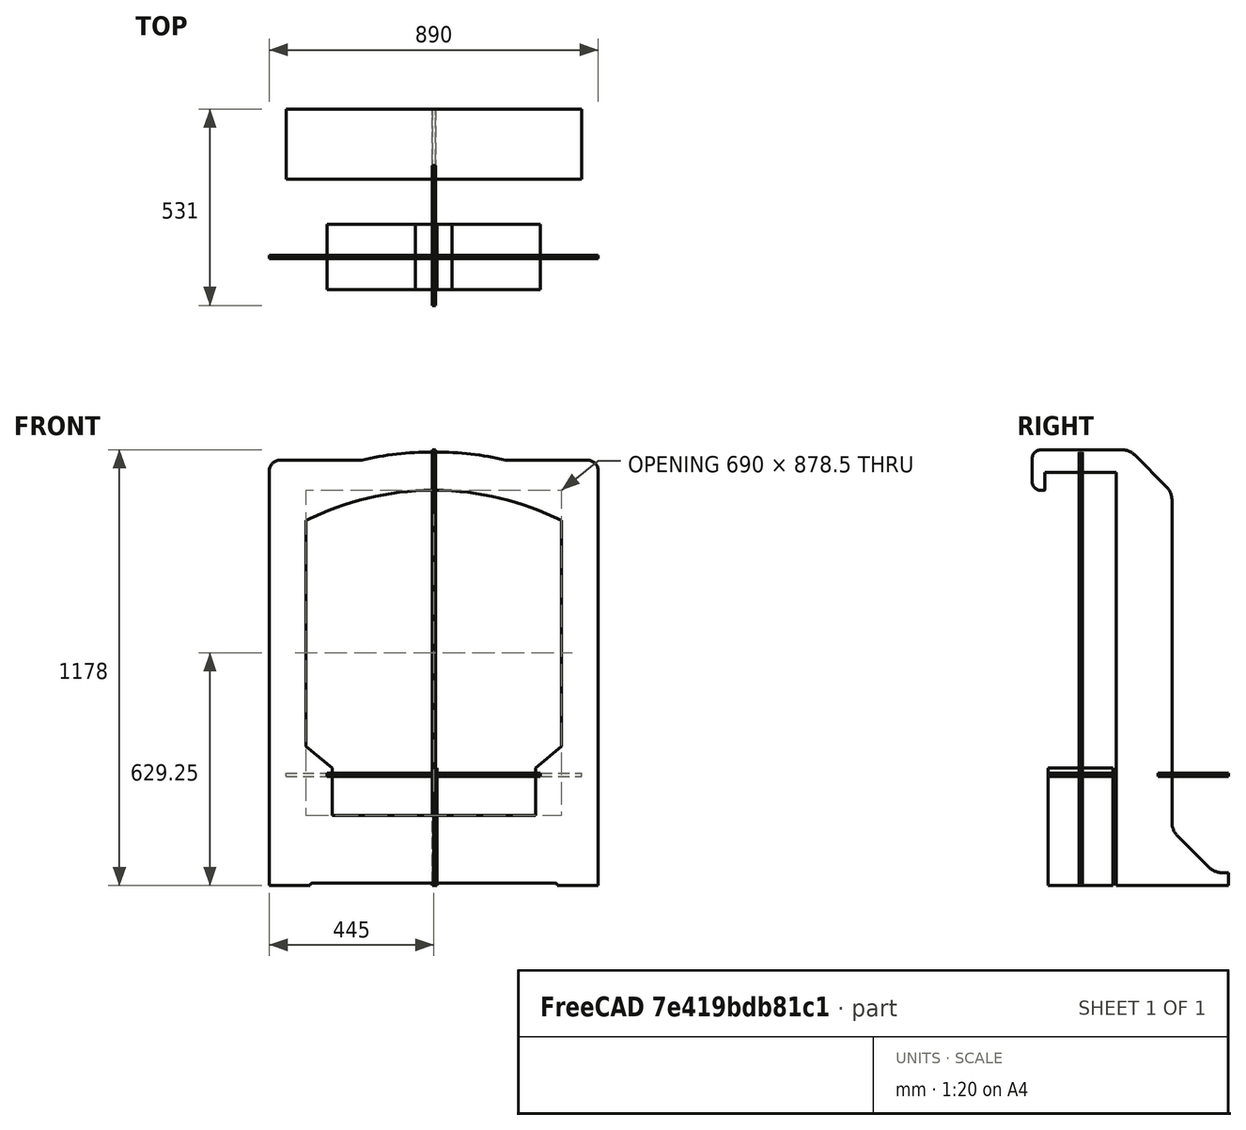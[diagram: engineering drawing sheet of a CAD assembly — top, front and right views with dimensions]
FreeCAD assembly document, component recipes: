
FREECAD ASSEMBLY — COMPONENT RECIPES ("Main_Assembly")

This assembly document has 9 components, labeled P0..P8 below (a component is one placed body or linked part). 8 of them carry a construction recipe — the FreeCAD feature program that regenerates the part from scratch, quoted from this document or its linked companion documents; the rest are supplied as boundary geometry only. No exploded tour is included for this assembly.
COMPONENT P0 — recipe-attached ("Back", modeled in this document).
Construction recipe (the document's own serialized feature program — sketch geometry with constraints, then the solid features built on it; lengths are millimeters unless a unit is written):

FEATURE [PartDesign::CoordinateSystem] LCS_0
  AttacherType = Attacher::AttachEngine3D
  MapMode = 2
  Support = -> [X_Axis002]
FEATURE [Sketcher::SketchObject] Sketch002  label="BackFrame_Sketch"
  FullyConstrained = true
  MapMode = 5
  Placement = pos=(0,0,0) rot=(1,0,0;1.5708rad)
  Support = -> [XZ_Plane002]
  expr: Constraints[57] = <<FrontFrame_Sketch>>.Constraints.height_base_B
  expr: Constraints[2] = 90 - <<key_dimensions>>#<<Dimensions>>.cradle_tilting
  expr: Constraints[66] = <<FrontFrame_Sketch>>.Constraints.foot_width
  expr: Constraints[17] = <<key_dimensions>>#<<Dimensions>>.window_width + <<key_dimensions>>#<<Dimensions>>.frame_width * 2
  expr: Constraints[22] = <<key_dimensions>>#<<Dimensions>>.window_width
  expr: Constraints[70] = <<key_dimensions>>#<<Dimensions>>.cradle_base
  expr: Constraints[33] = <<key_dimensions>>#<<Dimensions>>.top_height
  expr: Constraints[69] = <<key_dimensions>>#<<Dimensions>>.slider_axis_height
  expr: Constraints[8] = <<FrontFrame_Sketch>>.Constraints.lip_width
  expr: Constraints[16] = <<key_dimensions>>#<<Dimensions>>.center_height
  sketch-geometry (26):
    g0: LineSegment StartX=-252.795 StartY=212.12 StartZ=0 EndX=0 EndY=0 EndZ=0
    g1: LineSegment StartX=0 StartY=0 StartZ=0 EndX=252.795 EndY=212.12 EndZ=0
    g2: LineSegment StartX=-275 StartY=-64.25 StartZ=0 EndX=275 EndY=-64.25 EndZ=0
    g3: LineSegment StartX=-275 StartY=-109.25 StartZ=0 EndX=275 EndY=-109.25 EndZ=0
    g4: LineSegment StartX=-126.397 StartY=106.06 StartZ=0 EndX=452.112 EndY=795.5 EndZ=0
    g5: LineSegment StartX=126.397 StartY=106.06 StartZ=0 EndX=-452.112 EndY=795.5 EndZ=0
    g6: LineSegment StartX=-445 StartY=-299.25 StartZ=0 EndX=-334.5 EndY=-299.25 EndZ=0
    g7: ArcOfCircle CenterX=0 CenterY=0 CenterZ=0 NormalX=0 NormalY=0 NormalZ=1 AngleXU=0 Radius=769.25 StartAngle=1.10572 EndAngle=2.03587
    g8: LineSegment StartX=-445 StartY=-299.25 StartZ=0 EndX=-445 EndY=820.75 EndZ=0
    g9: LineSegment StartX=445 StartY=-299.25 StartZ=0 EndX=445 EndY=820.75 EndZ=0
    g10: ArcOfCircle CenterX=0 CenterY=0 CenterZ=0 NormalX=0 NormalY=0 NormalZ=1 AngleXU=0 Radius=872.75 StartAngle=1.34579 EndAngle=1.7958
    g11: LineSegment StartX=-415 StartY=850.75 StartZ=0 EndX=-194.723 EndY=850.75 EndZ=0
    g12: LineSegment StartX=194.723 StartY=850.75 StartZ=0 EndX=415 EndY=850.75 EndZ=0
    g13: GeomPoint X=-445 Y=850.75 Z=0
    g14: ArcOfCircle CenterX=-415 CenterY=820.75 CenterZ=0 NormalX=0 NormalY=0 NormalZ=1 AngleXU=0 Radius=30 StartAngle=1.5708 EndAngle=3.14159
    g15: ArcOfCircle CenterX=415 CenterY=820.75 CenterZ=0 NormalX=0 NormalY=0 NormalZ=1 AngleXU=0 Radius=30 StartAngle=9e-16 EndAngle=1.5708
    g16: LineSegment StartX=-345 StartY=687.547 StartZ=0 EndX=-345 EndY=77.487 EndZ=0
    g17: LineSegment StartX=-345 StartY=77.487 StartZ=0 EndX=-275 EndY=18.75 EndZ=0
    g18: LineSegment StartX=-275 StartY=18.75 StartZ=0 EndX=-275 EndY=-109.25 EndZ=0
    g19: LineSegment StartX=275 StartY=-109.25 StartZ=0 EndX=275 EndY=18.75 EndZ=0
    g20: LineSegment StartX=275 StartY=18.75 StartZ=0 EndX=345 EndY=77.487 EndZ=0
    g21: LineSegment StartX=345 StartY=77.487 StartZ=0 EndX=345 EndY=687.547 EndZ=0
    g22: ArcOfCircle CenterX=-327.5 CenterY=-299.25 CenterZ=0 NormalX=0 NormalY=0 NormalZ=1 AngleXU=0 Radius=7 StartAngle=1.5708 EndAngle=3.14159
    g23: ArcOfCircle CenterX=327.5 CenterY=-299.25 CenterZ=0 NormalX=0 NormalY=0 NormalZ=1 AngleXU=0 Radius=7 StartAngle=3.2e-15 EndAngle=1.5708
    g24: LineSegment StartX=-327.5 StartY=-292.25 StartZ=0 EndX=327.5 EndY=-292.25 EndZ=0
    g25: LineSegment StartX=334.5 StartY=-299.25 StartZ=0 EndX=445 EndY=-299.25 EndZ=0
  constraints (71):
    c: Coincident(g0,g-1)
    c: Distance(g0) = 330
    c: Angle(g-2,g0) = 0.872665
    c: Coincident(g1,g-1)
    c: Symmetric(g0,g1,g-2)
    c: DistanceY(g2,g-1) = 64.25
    c: Equal(g3,g2)
    c: Symmetric(g3,g3,g-2)
    c: DistanceX(g3,g3) = 550
    c: Symmetric(g2,g2,g-2)
    c: Perpendicular(g0,g4)
    c: Symmetric(g0,g-1,g4)
    c: Distance(g4) = 900
    c: Equal(g4,g5)
    c: Perpendicular(g1,g5)
    c: Symmetric(g-1,g1,g5)
    c: DistanceY(g25,g-1) = 299.25
    c: DistanceX(g6,g25) = 890
    c: Symmetric(g6,g25,g-2)
    c: Coincident(g7,g-1)
    c: Radius(g7) = 769.25
    c: Symmetric(g7,g7,g-2)
    c: DistanceX(g7,g7) = 690
    c: Coincident(g8,g6)
    c: Vertical(g8)
    c: Coincident(g9,g25)
    c: Vertical(g9)
    c: Coincident(g10,g-1)
    c: Coincident(g11,g10)
    c: Coincident(g12,g10)
    c: Tangent(g11,g12)
    c: Horizontal(g11)
    c: PointOnObject(g13,g11)
    c: DistanceY(g6,g13) = 1150
    c: Tangent(g8,g14) = 1.5708
    c: Tangent(g11,g14) = 1.5708
    c: Tangent(g12,g15) = 1.5708
    c: Tangent(g9,g15) = -1.5708
    c: Equal(g15,g14)
    c: Radius(g15) = 30
    c: Radius(g10) = 872.75
    c: Coincident(g16,g7)
    c: Vertical(g16)
    c: Coincident(g16,g17)
    c: Coincident(g17,g18)
    c: Coincident(g18,g3)
    c: Coincident(g3,g19)
    c: Vertical(g19)
    c: Coincident(g19,g20)
    c: Coincident(g20,g21)
    c: Coincident(g21,g7)
    c: Vertical(g21)
    c: Vertical(g18)
    c: Equal(g18,g19)
    c: DistanceY(g19,g10) = 109.25
    c: Parallel(g20,g1)
    c: Parallel(g17,g0)
    c: DistanceY(g6,g17) = 318
    c: PointOnObject(g22,g6)
    c: Horizontal(g24)
    c: Tangent(g24,g23) = 1.5708
    c: Tangent(g24,g22) = 1.5708
    c: Coincident(g6,g22)
    c: Coincident(g25,g23)
    c: Tangent(g6,g25)
    c: Symmetric(g22,g23,g-2)
    c: DistanceX(g6,g23) = 669
    c: Radius(g23) = 7
    c: PointOnObject(g13,g8)
    c: DistanceY(g9,g3) = 190
    c: DistanceY(g9,g2) = 235
FEATURE [PartDesign::Pad] Pad001
  Direction = (1,1,1)
  Length = 9
  Length2 = 100
  Midplane = true
  Placement = pos=(0,0,0) rot=(1,0,0;1.5708rad)
  Profile = -> Sketch002
  Type = 0
  expr: Length = <<key_dimensions>>#<<Dimensions>>.MDF_thick
FEATURE [PartDesign::Body] Back
  Group = -> [LCS_0,Sketch002,Pad001]
  Origin = -> Origin002
  Tip = -> Pad001
COMPONENT P1 — recipe-attached ("Back_Reinforcement", modeled in this document).
Construction recipe (the document's own serialized feature program — sketch geometry with constraints, then the solid features built on it; lengths are millimeters unless a unit is written):

FEATURE [PartDesign::CoordinateSystem] LCS_0006
  AttacherType = Attacher::AttachEngine3D
  MapMode = 2
  Support = -> [X_Axis008]
FEATURE [Sketcher::SketchObject] Sketch008
  FullyConstrained = true
  MapMode = 5
  Support = -> [XY_Plane008]
  sketch-geometry (6):
    g0: LineSegment StartX=-399.5 StartY=400 StartZ=0 EndX=399.5 EndY=400 EndZ=0
    g1: LineSegment StartX=399.5 StartY=400 StartZ=0 EndX=399.5 EndY=210 EndZ=0
    g2: LineSegment StartX=399.5 StartY=210 StartZ=0 EndX=-399.5 EndY=210 EndZ=0
    g3: LineSegment StartX=-399.5 StartY=210 StartZ=0 EndX=-399.5 EndY=400 EndZ=0
    g4: GeomPoint X=0 Y=305 Z=0
    g5: GeomPoint X=0 Y=400 Z=0
  constraints (15):
    c: Coincident(g0,g1)
    c: Coincident(g1,g2)
    c: Coincident(g2,g3)
    c: Coincident(g3,g0)
    c: Horizontal(g0)
    c: Horizontal(g2)
    c: Vertical(g1)
    c: Vertical(g3)
    c: PointOnObject(g4,g-2)
    c: Symmetric(g0,g1,g4)
    c: DistanceX(g0,g0) = 799
    c: DistanceY(g1,g1) = 190
    c: PointOnObject(g5,g0)
    c: DistanceY(g-1,g5) = 400
    c: PointOnObject(g5,g-2)
FEATURE [PartDesign::Pad] Pad007
  Direction = (1,1,1)
  Length = 9
  Length2 = 100
  Midplane = true
  Profile = -> Sketch008
  Type = 0
  expr: Length = <<key_dimensions>>#<<Dimensions>>.MDF_thick
FEATURE [PartDesign::Body] Back_Reinforcement
  Group = -> [LCS_0006,Sketch008,Pad007]
  Origin = -> Origin008
  Tip = -> Pad007
COMPONENT P2 — recipe-attached ("Front", modeled in this document).
Construction recipe (the document's own serialized feature program — sketch geometry with constraints, then the solid features built on it; lengths are millimeters unless a unit is written):

FEATURE [Sketcher::SketchObject] Sketch001  label="FrontFrame_Sketch"
  FullyConstrained = true
  MapMode = 5
  Placement = pos=(0,0,0) rot=(1,0,0;1.5708rad)
  Support = -> [XZ_Plane]
  expr: .Constraints.height_base_B = 318mm
  expr: Constraints[70] = <<key_dimensions>>#<<Dimensions>>.cradle_base
  expr: Constraints[22] = <<key_dimensions>>#<<Dimensions>>.window_width
  expr: Constraints[68] = <<key_dimensions>>#<<Dimensions>>.slider_axis_height
  expr: Constraints[16] = <<key_dimensions>>#<<Dimensions>>.center_height
  expr: Constraints[33] = <<key_dimensions>>#<<Dimensions>>.top_height
  expr: Constraints[2] = 90 - <<key_dimensions>>#<<Dimensions>>.cradle_tilting
  sketch-geometry (26):
    g0: LineSegment StartX=-252.795 StartY=212.12 StartZ=0 EndX=0 EndY=0 EndZ=0
    g1: LineSegment StartX=0 StartY=0 StartZ=0 EndX=252.795 EndY=212.12 EndZ=0
    g2: LineSegment StartX=-275 StartY=-64.25 StartZ=0 EndX=275 EndY=-64.25 EndZ=0
    g3: LineSegment StartX=-275 StartY=-109.25 StartZ=0 EndX=275 EndY=-109.25 EndZ=0
    g4: LineSegment StartX=-126.397 StartY=106.06 StartZ=0 EndX=452.112 EndY=795.5 EndZ=0
    g5: LineSegment StartX=126.397 StartY=106.06 StartZ=0 EndX=-452.112 EndY=795.5 EndZ=0
    g6: LineSegment StartX=-445 StartY=-299.25 StartZ=0 EndX=-334.5 EndY=-299.25 EndZ=0
    g7: ArcOfCircle CenterX=0 CenterY=0 CenterZ=0 NormalX=0 NormalY=0 NormalZ=1 AngleXU=0 Radius=769.25 StartAngle=1.10572 EndAngle=2.03587
    g8: LineSegment StartX=-445 StartY=-299.25 StartZ=0 EndX=-445 EndY=820.75 EndZ=0
    g9: LineSegment StartX=445 StartY=-299.25 StartZ=0 EndX=445 EndY=820.75 EndZ=0
    g10: ArcOfCircle CenterX=0 CenterY=0 CenterZ=0 NormalX=0 NormalY=0 NormalZ=1 AngleXU=0 Radius=872.75 StartAngle=1.34579 EndAngle=1.7958
    g11: LineSegment StartX=-415 StartY=850.75 StartZ=0 EndX=-194.723 EndY=850.75 EndZ=0
    g12: LineSegment StartX=194.723 StartY=850.75 StartZ=0 EndX=415 EndY=850.75 EndZ=0
    g13: GeomPoint X=-445 Y=850.75 Z=0
    g14: ArcOfCircle CenterX=-415 CenterY=820.75 CenterZ=0 NormalX=0 NormalY=0 NormalZ=1 AngleXU=0 Radius=30 StartAngle=1.5708 EndAngle=3.14159
    g15: ArcOfCircle CenterX=415 CenterY=820.75 CenterZ=0 NormalX=0 NormalY=0 NormalZ=1 AngleXU=0 Radius=30 StartAngle=1.4e-15 EndAngle=1.5708
    g16: LineSegment StartX=-345 StartY=687.547 StartZ=0 EndX=-345 EndY=77.487 EndZ=0
    g17: LineSegment StartX=-345 StartY=77.487 StartZ=0 EndX=-275 EndY=18.75 EndZ=0
    g18: LineSegment StartX=-275 StartY=18.75 StartZ=0 EndX=-275 EndY=-109.25 EndZ=0
    g19: LineSegment StartX=275 StartY=-109.25 StartZ=0 EndX=275 EndY=18.75 EndZ=0
    g20: LineSegment StartX=275 StartY=18.75 StartZ=0 EndX=345 EndY=77.487 EndZ=0
    g21: LineSegment StartX=345 StartY=77.487 StartZ=0 EndX=345 EndY=687.547 EndZ=0
    g22: ArcOfCircle CenterX=-327.5 CenterY=-299.25 CenterZ=0 NormalX=0 NormalY=0 NormalZ=1 AngleXU=0 Radius=7 StartAngle=1.5708 EndAngle=3.14159
    g23: ArcOfCircle CenterX=327.5 CenterY=-299.25 CenterZ=0 NormalX=0 NormalY=0 NormalZ=1 AngleXU=0 Radius=7 StartAngle=7.8e-15 EndAngle=1.5708
    g24: LineSegment StartX=-327.5 StartY=-292.25 StartZ=0 EndX=327.5 EndY=-292.25 EndZ=0
    g25: LineSegment StartX=334.5 StartY=-299.25 StartZ=0 EndX=445 EndY=-299.25 EndZ=0
  constraints (72):
    c: Coincident(g0,g-1)
    c: Distance(g0) = 330
    c: Angle(g-2,g0) = 0.872665
    c: Coincident(g1,g-1)
    c: Symmetric(g0,g1,g-2)
    c: DistanceY(g2,g-1) = 64.25
    c: Equal(g3,g2)
    c: Symmetric(g3,g3,g-2)
    c: DistanceX(g3,g3) = 550  'lip_width'
    c: Symmetric(g2,g2,g-2)
    c: Perpendicular(g0,g4)
    c: Symmetric(g0,g-1,g4)
    c: Distance(g4) = 900
    c: Equal(g4,g5)
    c: Perpendicular(g1,g5)
    c: Symmetric(g-1,g1,g5)
    c: DistanceY(g25,g-1) = 299.25
    c: DistanceX(g6,g25) = 890
    c: Symmetric(g6,g25,g-2)
    c: Coincident(g7,g-1)
    c: Radius(g7) = 769.25
    c: Symmetric(g7,g7,g-2)
    c: DistanceX(g7,g7) = 690
    c: Coincident(g8,g6)
    c: Vertical(g8)
    c: Coincident(g9,g25)
    c: Vertical(g9)
    c: Coincident(g10,g-1)
    c: Coincident(g11,g10)
    c: Coincident(g12,g10)
    c: Tangent(g11,g12)
    c: Horizontal(g11)
    c: PointOnObject(g13,g11)
    c: DistanceY(g6,g13) = 1150
    c: Tangent(g8,g14) = 1.5708
    c: Tangent(g11,g14) = 1.5708
    c: Tangent(g12,g15) = 1.5708
    c: Tangent(g9,g15) = -1.5708
    c: Equal(g15,g14)
    c: Radius(g15) = 30
    c: Radius(g10) = 872.75
    c: Coincident(g16,g7)
    c: Vertical(g16)
    c: Coincident(g16,g17)
    c: Coincident(g17,g18)
    c: Coincident(g18,g3)
    c: Coincident(g3,g19)
    c: Vertical(g19)
    c: Coincident(g19,g20)
    c: Coincident(g20,g21)
    c: Coincident(g21,g7)
    c: Vertical(g21)
    c: Vertical(g18)
    c: Equal(g18,g19)
    c: Parallel(g20,g1)
    c: Parallel(g17,g0)
    c: DistanceY(g6,g17) = 318  'height_base_B'
    c: PointOnObject(g22,g6)
    c: Equal(g23,g22)
    c: Coincident(g6,g22)
    c: Coincident(g25,g23)
    c: Tangent(g6,g25)
    c: Radius(g22) = 7  'foot_radius'
    c: DistanceX(g6,g23) = 669  'foot_width'
    c: Tangent(g24,g22) = 1.5708
    c: Tangent(g24,g23) = 1.5708
    c: Symmetric(g22,g23,g-2)
    c: PointOnObject(g13,g8)
    c: DistanceY(g9,g3) = 190
    c: DistanceY(g3,g7) = 109.25
    c: DistanceY(g9,g2) = 235
    c: DistanceY(g3,g2) = 45
FEATURE [PartDesign::Pad] Pad
  Direction = (1,1,1)
  Length = 9
  Length2 = 100
  Midplane = true
  Placement = pos=(0,0,0) rot=(1,0,0;1.5708rad)
  Profile = -> Sketch001
  Type = 0
  expr: Length = <<key_dimensions>>#<<Dimensions>>.MDF_thick
FEATURE [PartDesign::CoordinateSystem] LCS_Front_1
  AttacherType = Attacher::AttachEngine3D
  MapMode = 5
  Support = -> [XY_Plane]
FEATURE [PartDesign::Body] Body  label="Front"
  Group = -> [Sketch001,Pad,LCS_Front_1]
  Origin = -> Origin
  Tip = -> Pad
COMPONENT P3 — recipe-attached ("Column_left", modeled in this document).
Construction recipe (the document's own serialized feature program — sketch geometry with constraints, then the solid features built on it; lengths are millimeters unless a unit is written):

FEATURE [PartDesign::CoordinateSystem] LCS_0004
  AttacherType = Attacher::AttachEngine3D
  MapMode = 2
  Support = -> [X_Axis006]
FEATURE [Sketcher::SketchObject] Sketch006  label="Column_left_Sketch"
  FullyConstrained = true
  MapMode = 5
  Placement = pos=(0,0,0) rot=(0.57735,0.57735,0.57735;2.0944rad)
  Support = -> [YZ_Plane006]
  expr: Constraints[56] = <<Column_right_Sketch>>.Constraints.front_height
  expr: Constraints[50] = <<Column_right_Sketch>>.Constraints.radius_small
  expr: Constraints[34] = <<Column_right_Sketch>>.Constraints.radius_big
  expr: Constraints[45] = <<Column_right_Sketch>>.Constraints.oblique_length
  expr: Constraints[20] = <<Column_right_Sketch>>.Constraints.column_width
  expr: Constraints[65] = <<key_dimensions>>#<<Dimensions>>.rear_overhang
  expr: Constraints[23] = <<key_dimensions>>#<<Dimensions>>.center_height
  expr: Constraints[26] = <<key_dimensions>>#<<Dimensions>>.top_height - 33
  expr: Constraints[60] = <<key_dimensions>>#<<Dimensions>>.frame_depth / 2 + <<key_dimensions>>#<<Dimensions>>.MDF_thick
  expr: Constraints[25] = <<Dimensions>>.foot_height
  expr: Constraints[21] = <<key_dimensions>>#<<Dimensions>>.frame_depth / 2 + <<key_dimensions>>#<<Dimensions>>.MDF_thick
  sketch-geometry (23):
    g0: LineSegment StartX=97 StartY=-299.25 StartZ=0 EndX=97 EndY=817.75 EndZ=0
    g1: LineSegment StartX=97 StartY=817.75 StartZ=0 EndX=-97 EndY=817.75 EndZ=0
    g2: LineSegment StartX=-97 StartY=817.75 StartZ=0 EndX=-97 EndY=770.75 EndZ=0
    g3: LineSegment StartX=-99 StartY=768.75 StartZ=0 EndX=-106 EndY=768.75 EndZ=0
    g4: LineSegment StartX=-131 StartY=793.75 StartZ=0 EndX=-131 EndY=853.75 EndZ=0
    g5: LineSegment StartX=-106 StartY=878.75 StartZ=0 EndX=111.44 EndY=878.75 EndZ=0
    g6: LineSegment StartX=146.795 StartY=864.105 StartZ=0 EndX=232.355 EndY=778.545 EndZ=0
    g7: LineSegment StartX=247 StartY=743.19 StartZ=0 EndX=247 EndY=-128.69 EndZ=0
    g8: LineSegment StartX=261.645 StartY=-164.045 StartZ=0 EndX=347.205 EndY=-249.605 EndZ=0
    g9: LineSegment StartX=382.56 StartY=-264.25 StartZ=0 EndX=400 EndY=-264.25 EndZ=0
    g10: LineSegment StartX=400 StartY=-264.25 StartZ=0 EndX=400 EndY=-299.25 EndZ=0
    g11: LineSegment StartX=400 StartY=-299.25 StartZ=0 EndX=97 EndY=-299.25 EndZ=0
    g12: LineSegment StartX=97 StartY=0 StartZ=0 EndX=247 EndY=0 EndZ=0
    g13: ArcOfCircle CenterX=111.44 CenterY=828.75 CenterZ=0 NormalX=0 NormalY=0 NormalZ=1 AngleXU=0 Radius=50 StartAngle=0.785398 EndAngle=1.5708
    g14: ArcOfCircle CenterX=197 CenterY=743.19 CenterZ=0 NormalX=0 NormalY=0 NormalZ=1 AngleXU=0 Radius=50 StartAngle=-9e-16 EndAngle=0.785398
    g15: ArcOfCircle CenterX=297 CenterY=-128.69 CenterZ=0 NormalX=0 NormalY=0 NormalZ=1 AngleXU=0 Radius=50 StartAngle=3.14159 EndAngle=3.92699
    g16: ArcOfCircle CenterX=382.56 CenterY=-214.25 CenterZ=0 NormalX=0 NormalY=0 NormalZ=1 AngleXU=0 Radius=50 StartAngle=3.92699 EndAngle=4.71239
    g17: LineSegment StartX=0 StartY=878.75 StartZ=0 EndX=0 EndY=817.75 EndZ=0
    g18: ArcOfCircle CenterX=-106 CenterY=853.75 CenterZ=0 NormalX=0 NormalY=0 NormalZ=1 AngleXU=0 Radius=25 StartAngle=1.5708 EndAngle=3.14159
    g19: ArcOfCircle CenterX=-106 CenterY=793.75 CenterZ=0 NormalX=0 NormalY=0 NormalZ=1 AngleXU=0 Radius=25 StartAngle=3.14159 EndAngle=4.71239
    g20: LineSegment StartX=-131 StartY=817.75 StartZ=0 EndX=-97 EndY=817.75 EndZ=0
    g21: LineSegment StartX=-97 StartY=793.75 StartZ=0 EndX=0 EndY=793.75 EndZ=0
    g22: ArcOfCircle CenterX=-99 CenterY=770.75 CenterZ=0 NormalX=0 NormalY=0 NormalZ=1 AngleXU=0 Radius=2 StartAngle=4.71239 EndAngle=6.28319
  constraints (66):
    c: Vertical(g0)
    c: Coincident(g0,g1)
    c: Horizontal(g1)
    c: Coincident(g1,g2)
    c: Vertical(g2)
    c: Horizontal(g3)
    c: Vertical(g4)
    c: Horizontal(g5)
    c: Vertical(g7)
    c: Coincident(g9,g10)
    c: Vertical(g10)
    c: Coincident(g10,g11)
    c: Coincident(g11,g0)
    c: Horizontal(g11)
    c: Horizontal(g9)
    c: Parallel(g6,g8)
    c: Angle(g6) = -0.785398
    c: PointOnObject(g12,g0)
    c: PointOnObject(g12,g7)
    c: Horizontal(g12)
    c: DistanceX(g12,g12) = 150
    c: DistanceX(g-1,g12) = 97
    c: PointOnObject(g12,g-1)
    c: DistanceY(g0,g-1) = 299.25
    c: DistanceX(g11,g11) = 303
    c: DistanceY(g10,g10) = 35
    c: DistanceY(g0,g0) = 1117
    c: Equal(g8,g6)
    c: Tangent(g5,g13) = 1.5708
    c: Tangent(g6,g13) = 1.5708
    c: Tangent(g6,g14) = 1.5708
    c: Tangent(g7,g14) = 1.5708
    c: Tangent(g7,g15) = -1.5708
    c: Tangent(g8,g15) = -1.5708
    c: Radius(g14) = 50
    c: Equal(g13,g14)
    c: Equal(g15,g14)
    c: Tangent(g8,g16) = -1.5708
    c: Tangent(g9,g16) = -1.5708
    c: Equal(g16,g15)
    c: PointOnObject(g17,g5)
    c: PointOnObject(g17,g1)
    c: Vertical(g17)
    c: DistanceY(g17,g17) = 61
    c: PointOnObject(g17,g-2)
    c: Distance(g6) = 121
    c: Tangent(g5,g18) = 1.5708
    c: Tangent(g4,g18) = 1.5708
    c: Tangent(g4,g19) = 1.5708
    c: Tangent(g3,g19) = 1.5708
    c: Radius(g19) = 25
    c: Equal(g18,g19)
    c: PointOnObject(g20,g4)
    c: Coincident(g20,g1)
    c: Horizontal(g20)
    c: DistanceX(g20,g20) = 34
    c: DistanceY(g3,g5) = 110
    c: PointOnObject(g21,g2)
    c: PointOnObject(g21,g-2)
    c: Horizontal(g21)
    c: DistanceX(g21,g21) = 97
    c: PointOnObject(g4,g21)
    c: Tangent(g3,g22) = 1.5708
    c: Tangent(g2,g22) = 1.5708
    c: Radius(g22) = 2
    c: DistanceX(g-1,g10) = 400
FEATURE [PartDesign::Pad] Pad005
  Direction = (1,1,1)
  Length = 9
  Length2 = 100
  Midplane = true
  Placement = pos=(0,0,0) rot=(0.57735,0.57735,0.57735;2.0944rad)
  Profile = -> Sketch006
  Type = 0
  expr: Length = <<key_dimensions>>#<<Dimensions>>.MDF_thick
FEATURE [PartDesign::Body] Column_left
  Group = -> [LCS_0004,Sketch006,Pad005]
  Origin = -> Origin006
  Tip = -> Pad005
COMPONENT P4 — recipe-attached ("Column_right", modeled in this document).
Construction recipe (the document's own serialized feature program — sketch geometry with constraints, then the solid features built on it; lengths are millimeters unless a unit is written):

FEATURE [PartDesign::CoordinateSystem] LCS_0003
  AttacherType = Attacher::AttachEngine3D
  MapMode = 2
  Support = -> [X_Axis005]
FEATURE [Sketcher::SketchObject] Sketch005  label="Column_right_Sketch"
  FullyConstrained = true
  MapMode = 5
  Placement = pos=(0,0,0) rot=(0.57735,0.57735,0.57735;2.0944rad)
  Support = -> [YZ_Plane005]
  expr: Constraints[25] = <<Dimensions>>.foot_height
  expr: Constraints[21] = <<key_dimensions>>#<<Dimensions>>.frame_depth / 2 + <<key_dimensions>>#<<Dimensions>>.MDF_thick
  expr: Constraints[26] = <<key_dimensions>>#<<Dimensions>>.top_height - 33
  expr: Constraints[60] = <<key_dimensions>>#<<Dimensions>>.frame_depth / 2 + <<key_dimensions>>#<<Dimensions>>.MDF_thick
  expr: Constraints[23] = <<key_dimensions>>#<<Dimensions>>.center_height
  expr: Constraints[65] = <<key_dimensions>>#<<Dimensions>>.rear_overhang
  sketch-geometry (23):
    g0: LineSegment StartX=97 StartY=-299.25 StartZ=0 EndX=97 EndY=817.75 EndZ=0
    g1: LineSegment StartX=97 StartY=817.75 StartZ=0 EndX=-97 EndY=817.75 EndZ=0
    g2: LineSegment StartX=-97 StartY=817.75 StartZ=0 EndX=-97 EndY=770.75 EndZ=0
    g3: LineSegment StartX=-99 StartY=768.75 StartZ=0 EndX=-106 EndY=768.75 EndZ=0
    g4: LineSegment StartX=-131 StartY=793.75 StartZ=0 EndX=-131 EndY=853.75 EndZ=0
    g5: LineSegment StartX=-106 StartY=878.75 StartZ=0 EndX=111.44 EndY=878.75 EndZ=0
    g6: LineSegment StartX=146.795 StartY=864.105 StartZ=0 EndX=232.355 EndY=778.545 EndZ=0
    g7: LineSegment StartX=247 StartY=743.19 StartZ=0 EndX=247 EndY=-128.69 EndZ=0
    g8: LineSegment StartX=261.645 StartY=-164.045 StartZ=0 EndX=347.205 EndY=-249.605 EndZ=0
    g9: LineSegment StartX=382.56 StartY=-264.25 StartZ=0 EndX=400 EndY=-264.25 EndZ=0
    g10: LineSegment StartX=400 StartY=-264.25 StartZ=0 EndX=400 EndY=-299.25 EndZ=0
    g11: LineSegment StartX=400 StartY=-299.25 StartZ=0 EndX=97 EndY=-299.25 EndZ=0
    g12: LineSegment StartX=97 StartY=0 StartZ=0 EndX=247 EndY=0 EndZ=0
    g13: ArcOfCircle CenterX=111.44 CenterY=828.75 CenterZ=0 NormalX=0 NormalY=0 NormalZ=1 AngleXU=0 Radius=50 StartAngle=0.785398 EndAngle=1.5708
    g14: ArcOfCircle CenterX=197 CenterY=743.19 CenterZ=0 NormalX=0 NormalY=0 NormalZ=1 AngleXU=0 Radius=50 StartAngle=-9e-16 EndAngle=0.785398
    g15: ArcOfCircle CenterX=297 CenterY=-128.69 CenterZ=0 NormalX=0 NormalY=0 NormalZ=1 AngleXU=0 Radius=50 StartAngle=3.14159 EndAngle=3.92699
    g16: ArcOfCircle CenterX=382.56 CenterY=-214.25 CenterZ=0 NormalX=0 NormalY=0 NormalZ=1 AngleXU=0 Radius=50 StartAngle=3.92699 EndAngle=4.71239
    g17: LineSegment StartX=0 StartY=878.75 StartZ=0 EndX=0 EndY=817.75 EndZ=0
    g18: ArcOfCircle CenterX=-106 CenterY=853.75 CenterZ=0 NormalX=0 NormalY=0 NormalZ=1 AngleXU=0 Radius=25 StartAngle=1.5708 EndAngle=3.14159
    g19: ArcOfCircle CenterX=-106 CenterY=793.75 CenterZ=0 NormalX=0 NormalY=0 NormalZ=1 AngleXU=0 Radius=25 StartAngle=3.14159 EndAngle=4.71239
    g20: LineSegment StartX=-131 StartY=817.75 StartZ=0 EndX=-97 EndY=817.75 EndZ=0
    g21: LineSegment StartX=-97 StartY=793.75 StartZ=0 EndX=0 EndY=793.75 EndZ=0
    g22: ArcOfCircle CenterX=-99 CenterY=770.75 CenterZ=0 NormalX=0 NormalY=0 NormalZ=1 AngleXU=0 Radius=2 StartAngle=4.71239 EndAngle=6.28319
  constraints (66):
    c: Vertical(g0)
    c: Coincident(g0,g1)
    c: Horizontal(g1)
    c: Coincident(g1,g2)
    c: Vertical(g2)
    c: Horizontal(g3)
    c: Vertical(g4)
    c: Horizontal(g5)
    c: Vertical(g7)
    c: Coincident(g9,g10)
    c: Vertical(g10)
    c: Coincident(g10,g11)
    c: Coincident(g11,g0)
    c: Horizontal(g11)
    c: Horizontal(g9)
    c: Parallel(g6,g8)
    c: Angle(g6) = -0.785398
    c: PointOnObject(g12,g0)
    c: PointOnObject(g12,g7)
    c: Horizontal(g12)
    c: DistanceX(g12,g12) = 150  'column_width'
    c: DistanceX(g-1,g12) = 97
    c: PointOnObject(g12,g-1)
    c: DistanceY(g0,g-1) = 299.25
    c: DistanceX(g11,g11) = 303
    c: DistanceY(g10,g10) = 35
    c: DistanceY(g0,g0) = 1117
    c: Equal(g8,g6)
    c: Tangent(g5,g13) = 1.5708
    c: Tangent(g6,g13) = 1.5708
    c: Tangent(g6,g14) = 1.5708
    c: Tangent(g7,g14) = 1.5708
    c: Tangent(g7,g15) = -1.5708
    c: Tangent(g8,g15) = -1.5708
    c: Radius(g14) = 50  'radius_big'
    c: Equal(g13,g14)
    c: Equal(g15,g14)
    c: Tangent(g8,g16) = -1.5708
    c: Tangent(g9,g16) = -1.5708
    c: Equal(g16,g15)
    c: PointOnObject(g17,g5)
    c: PointOnObject(g17,g1)
    c: Vertical(g17)
    c: DistanceY(g17,g17) = 61
    c: PointOnObject(g17,g-2)
    c: Distance(g6) = 121  'oblique_length'
    c: Tangent(g5,g18) = 1.5708
    c: Tangent(g4,g18) = 1.5708
    c: Tangent(g4,g19) = 1.5708
    c: Tangent(g3,g19) = 1.5708
    c: Radius(g19) = 25  'radius_small'
    c: Equal(g18,g19)
    c: PointOnObject(g20,g4)
    c: Coincident(g20,g1)
    c: Horizontal(g20)
    c: DistanceX(g20,g20) = 34
    c: DistanceY(g3,g5) = 110  'front_height'
    c: PointOnObject(g21,g2)
    c: PointOnObject(g21,g-2)
    c: Horizontal(g21)
    c: DistanceX(g21,g21) = 97
    c: PointOnObject(g4,g21)
    c: Tangent(g3,g22) = 1.5708
    c: Tangent(g2,g22) = 1.5708
    c: Radius(g22) = 2
    c: DistanceX(g-1,g10) = 400
FEATURE [PartDesign::Pad] Pad004
  Direction = (1,1,1)
  Length = 9
  Length2 = 100
  Midplane = true
  Placement = pos=(0,0,0) rot=(0.57735,0.57735,0.57735;2.0944rad)
  Profile = -> Sketch005
  Type = 0
  expr: Length = <<key_dimensions>>#<<Dimensions>>.MDF_thick
FEATURE [PartDesign::Body] Column_right
  Group = -> [LCS_0003,Sketch005,Pad004]
  Origin = -> Origin005
  Tip = -> Pad004
COMPONENT P5 — recipe-attached ("Lid", modeled in this document).
Construction recipe (the document's own serialized feature program — sketch geometry with constraints, then the solid features built on it; lengths are millimeters unless a unit is written):

FEATURE [PartDesign::CoordinateSystem] LCS_0005
  AttacherType = Attacher::AttachEngine3D
  MapMode = 2
  Support = -> [X_Axis007]
FEATURE [Sketcher::SketchObject] Sketch007
  FullyConstrained = true
  MapMode = 5
  Support = -> [XY_Plane007]
  expr: Constraints[9] = <<key_dimensions>>#<<Dimensions>>.frame_depth
  sketch-geometry (4):
    g0: LineSegment StartX=-288 StartY=88 StartZ=0 EndX=288 EndY=88 EndZ=0
    g1: LineSegment StartX=288 StartY=88 StartZ=0 EndX=288 EndY=-88 EndZ=0
    g2: LineSegment StartX=288 StartY=-88 StartZ=0 EndX=-288 EndY=-88 EndZ=0
    g3: LineSegment StartX=-288 StartY=-88 StartZ=0 EndX=-288 EndY=88 EndZ=0
  constraints (11):
    c: Coincident(g0,g1)
    c: Coincident(g1,g2)
    c: Coincident(g2,g3)
    c: Coincident(g3,g0)
    c: Horizontal(g0)
    c: Horizontal(g2)
    c: Vertical(g1)
    c: Vertical(g3)
    c: Symmetric(g0,g2,g-1)
    c: DistanceY(g3,g3) = 176
    c: DistanceX(g2,g2) = 576
FEATURE [PartDesign::Pad] Pad006
  Direction = (1,1,1)
  Length = 9
  Length2 = 100
  Midplane = true
  Profile = -> Sketch007
  Type = 0
  expr: Length = <<key_dimensions>>#<<Dimensions>>.MDF_thick
FEATURE [PartDesign::Body] Lid
  Group = -> [LCS_0005,Sketch007,Pad006]
  Origin = -> Origin007
  Tip = -> Pad006
COMPONENT P6 — geometry summary ("Model"; no construction recipe available for this part):
  bounding box: 1178.0 x 890.0 x 560.0 mm
  tessellated surface: 1,232 triangles
  volume: 21112579395300267166470914615812202629443498102417788420728207165643623480000163467339874629170430476288 mm^3 (3595985829578295630362537329748754173144165194598282095387554917623151073899522194275030425141248% of its bounding box)
COMPONENT P7 — recipe-attached ("Side", modeled in this document).
Construction recipe (the document's own serialized feature program — sketch geometry with constraints, then the solid features built on it; lengths are millimeters unless a unit is written):

FEATURE [PartDesign::CoordinateSystem] LCS_0001
  AttacherType = Attacher::AttachEngine3D
  MapMode = 2
  Support = -> [X_Axis003]
FEATURE [Sketcher::SketchObject] Sketch003  label="Side_Sketch"
  FullyConstrained = true
  MapMode = 5
  Placement = pos=(0,0,0) rot=(0.57735,0.57735,0.57735;2.0944rad)
  Support = -> [YZ_Plane003]
  sketch-geometry (6):
    g0: LineSegment StartX=-88 StartY=18.75 StartZ=0 EndX=88 EndY=18.75 EndZ=0
    g1: LineSegment StartX=88 StartY=18.75 StartZ=0 EndX=88 EndY=-299.25 EndZ=0
    g2: LineSegment StartX=88 StartY=-299.25 StartZ=0 EndX=-88 EndY=-299.25 EndZ=0
    g3: LineSegment StartX=-88 StartY=-299.25 StartZ=0 EndX=-88 EndY=18.75 EndZ=0
    g4: GeomPoint X=0 Y=-299.25 Z=0
    g5: LineSegment StartX=0 StartY=18.75 StartZ=0 EndX=0 EndY=-299.25 EndZ=0
  constraints (17):
    c: Coincident(g0,g1)
    c: Coincident(g1,g2)
    c: Coincident(g2,g3)
    c: Coincident(g3,g0)
    c: Horizontal(g0)
    c: Horizontal(g2)
    c: Vertical(g1)
    c: Vertical(g3)
    c: DistanceX(g0,g0) = 176
    c: DistanceY(g1,g-1) = 299.25
    c: Symmetric(g2,g1,g4)
    c: PointOnObject(g4,g-2)
    c: PointOnObject(g5,g0)
    c: PointOnObject(g5,g2)
    c: Vertical(g5)
    c: DistanceY(g5,g5) = 318
    c: PointOnObject(g5,g-2)
FEATURE [PartDesign::Pad] Pad002
  Direction = (1,1,1)
  Length = 9
  Length2 = 100
  Placement = pos=(0,0,0) rot=(0.57735,0.57735,0.57735;2.0944rad)
  Profile = -> Sketch003
  Type = 0
  expr: Length = <<key_dimensions>>#<<Dimensions>>.MDF_thick
FEATURE [PartDesign::Body] Side
  Group = -> [LCS_0001,Sketch003,Pad002]
  Origin = -> Origin003
  Tip = -> Pad002
COMPONENT P8 — recipe-attached ("Side_Reinforcement", modeled in this document).
Construction recipe (the document's own serialized feature program — sketch geometry with constraints, then the solid features built on it; lengths are millimeters unless a unit is written):

FEATURE [PartDesign::CoordinateSystem] LCS_0002
  AttacherType = Attacher::AttachEngine3D
  MapMode = 2
  Support = -> [X_Axis004]
FEATURE [Sketcher::SketchObject] Sketch004  label="Side_Reinforcement_Sketch"
  FullyConstrained = true
  MapMode = 5
  Support = -> [XY_Plane004]
  expr: Constraints[8] = <<key_dimensions>>#<<Dimensions>>.frame_depth
  sketch-geometry (5):
    g0: LineSegment StartX=-50 StartY=88 StartZ=0 EndX=50 EndY=88 EndZ=0
    g1: LineSegment StartX=50 StartY=88 StartZ=0 EndX=50 EndY=-88 EndZ=0
    g2: LineSegment StartX=50 StartY=-88 StartZ=0 EndX=-50 EndY=-88 EndZ=0
    g3: LineSegment StartX=-50 StartY=-88 StartZ=0 EndX=-50 EndY=88 EndZ=0
    g4: LineSegment StartX=-50 StartY=0 StartZ=0 EndX=50 EndY=0 EndZ=0
  constraints (15):
    c: Coincident(g0,g1)
    c: Coincident(g1,g2)
    c: Coincident(g2,g3)
    c: Coincident(g3,g0)
    c: Horizontal(g0)
    c: Horizontal(g2)
    c: Vertical(g1)
    c: Vertical(g3)
    c: DistanceY(g3,g3) = 176
    c: Symmetric(g0,g2,g-1)
    c: PointOnObject(g4,g3)
    c: PointOnObject(g4,g1)
    c: Horizontal(g4)
    c: DistanceX(g4,g4) = 100
    c: PointOnObject(g4,g-1)
FEATURE [PartDesign::Pad] Pad003
  Direction = (1,1,1)
  Length = 9
  Length2 = 100
  Midplane = true
  Profile = -> Sketch004
  Type = 0
  expr: Length = <<key_dimensions>>#<<Dimensions>>.MDF_thick
FEATURE [PartDesign::Body] Side_Reinforcement
  Group = -> [LCS_0002,Sketch004,Pad003]
  Origin = -> Origin004
  Tip = -> Pad003
PROVENANCE & LICENSES
A FreeCAD (.FCStd) document from a public repository crawl; recipes are the document's own serialized feature recipes (and, for linked parts, companion documents' recipes).
License: cc-by-sa-4.0.
